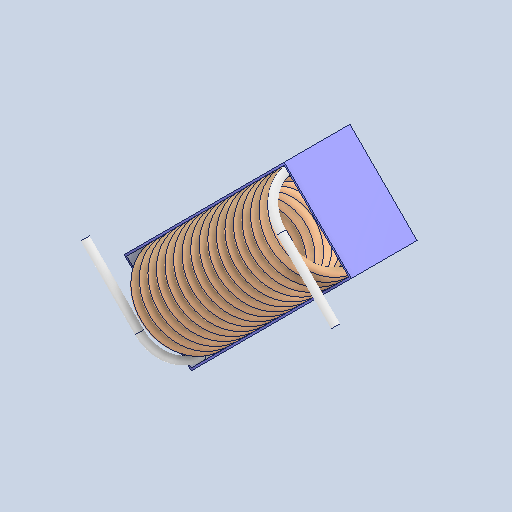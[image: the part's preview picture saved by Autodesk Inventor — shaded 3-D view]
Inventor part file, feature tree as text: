
AUTODESK INVENTOR PART (.ipt)
format: ipt  version: 2025 (Build 290162000, 162)  size: 711,680 bytes
history: native  units: mm
features: sweep x1, other x1
ambient origin geometry x8: Origin, YZ Plane, XZ Plane, XY Plane, X Axis, Y Axis, Z Axis, Center Point
bodies: Solid1 (feature_tree), Solid2 (feature_tree)
feature tree (2):
  sweep  "Sweep9"
  other  "Cut-Extrude1"
